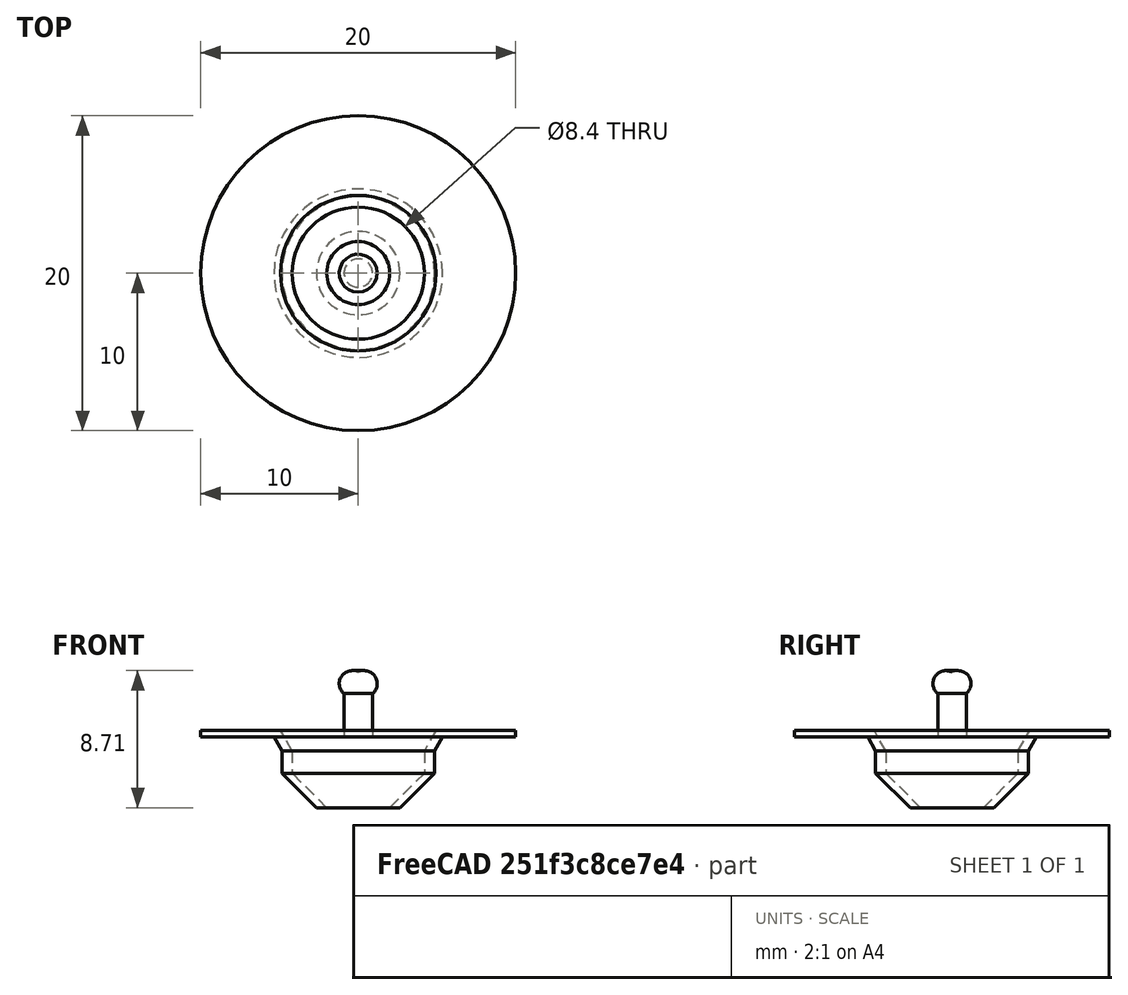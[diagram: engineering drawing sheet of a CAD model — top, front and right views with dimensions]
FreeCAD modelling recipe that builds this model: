
FCSTD DOCUMENT  (FreeCAD 0.15R4671 (Git))
Label: v4
License: CC-BY 3.0
LicenseURL: http://creativecommons.org/licenses/by/3.0/
objects: Sketcher::SketchObject×20, PartDesign::Revolution×14, App::MeasureDistance×2, Mesh::Feature×1, App::DocumentObjectGroup×1
note: 48 computed .brp shape members not serialized (recipe doc carries the construction recipe); baked Part::Feature solids carry a one-line shape summary decoded from their .brp

FEATURE [Mesh::Feature] M2_Electrode_Mount_B_01  label="M2_Electrode Mount B_01"
FEATURE [Sketcher::SketchObject] Sketch
  sketch-geometry (2):
    g0: Circle CenterX=0 CenterY=0 CenterZ=0 NormalX=0 NormalY=0 NormalZ=1 Radius=5.35
    g1: Circle CenterX=0 CenterY=0 CenterZ=0 NormalX=0 NormalY=0 NormalZ=1 Radius=10
  constraints (2):
    c: Coincident(g0,g-1)
    c: Coincident(g1,g-1)
FEATURE [Sketcher::SketchObject] Sketch001
  Placement = pos=(0,0,-0.9) rot=(0,0,1;0rad)
  sketch-geometry (1):
    g0: Circle CenterX=0 CenterY=0 CenterZ=0 NormalX=0 NormalY=0 NormalZ=1 Radius=4.85008
  constraints (1):
    c: Coincident(g0,g-1)
FEATURE [Sketcher::SketchObject] Sketch002
  Placement = pos=(0,0,-2.3) rot=(0,0,1;0rad)
  sketch-geometry (1):
    g0: Circle CenterX=0 CenterY=0 CenterZ=0 NormalX=0 NormalY=0 NormalZ=1 Radius=4.85
  constraints (1):
    c: Coincident(g0,g-1)
FEATURE [Sketcher::SketchObject] Sketch004
  Placement = pos=(0,0,-4.5) rot=(0,0,1;0rad)
  sketch-geometry (2):
    g0: Circle CenterX=0 CenterY=0 CenterZ=0 NormalX=0 NormalY=0 NormalZ=1 Radius=2.65073
    g1: Circle CenterX=0 CenterY=0 CenterZ=0 NormalX=0 NormalY=0 NormalZ=1 Radius=2.00003
  constraints (2):
    c: Coincident(g0,g-1)
    c: Coincident(g1,g-1)
FEATURE [Sketcher::SketchObject] Sketch005
  Placement = pos=(0,0,0) rot=(1,0,0;1.5708rad)
  sketch-geometry (10):
    g0: LineSegment StartX=2 StartY=-4.5 StartZ=0 EndX=2.65074 EndY=-4.5 EndZ=0
    g1: LineSegment StartX=2.65074 StartY=-4.5 StartZ=0 EndX=4.85006 EndY=-2.29993 EndZ=0
    g2: LineSegment StartX=4.85006 StartY=-2.29993 StartZ=0 EndX=4.85006 EndY=-0.900001 EndZ=0
    g3: LineSegment StartX=4.85006 StartY=-0.900001 StartZ=0 EndX=5.35009 EndY=0 EndZ=0
    g4: LineSegment StartX=5.35009 StartY=0 StartZ=0 EndX=10 EndY=0 EndZ=0
    g5: LineSegment StartX=10 StartY=0 StartZ=0 EndX=10 EndY=0.428388 EndZ=0
    g6: LineSegment StartX=10 StartY=0.428388 StartZ=0 EndX=4.93781 EndY=0.428388 EndZ=0
    g7: LineSegment StartX=4.93781 StartY=0.428388 StartZ=0 EndX=4.19944 EndY=-0.900596 EndZ=0
    g8: LineSegment StartX=4.19944 StartY=-0.900596 StartZ=0 EndX=4.19944 EndY=-2.29981 EndZ=0
    g9: LineSegment StartX=4.19944 StartY=-2.29981 StartZ=0 EndX=2 EndY=-4.5 EndZ=0
  constraints (28):
    c: Coincident(g0,g1)
    c: Coincident(g1,g2)
    c: Coincident(g2,g3)
    c: Coincident(g3,g4)
    c: Coincident(g4,g5)
    c: Coincident(g5,g6)
    c: Coincident(g6,g7)
    c: Coincident(g7,g8)
    c: Coincident(g8,g9)
    c: Coincident(g9,g0)
    c: Parallel(g6,g4)
    c: Parallel(g4,g0)
    c: Parallel(g5,g2)
    c: Parallel(g2,g8)
    c: Perpendicular(g0,g5)
    c: PointOnObject(g3,g-1)
    c: Parallel(g9,g1)
    c: Parallel(g7,g3)
    c: DistanceX(g0) = 2
    c: DistanceY(g0) = -4.5
    c: DistanceX(g4) = 10
    c: DistanceX(g0) = 2.65074
    c: DistanceY(g0) = -4.5
    c: DistanceX(g1) = 4.85006
    c: DistanceY(g1) = -2.29993
    c: DistanceY(g2) = -0.900001
    c: DistanceX(g3) = 5.35009
    c: DistanceX(g8) = 4.19944
FEATURE [PartDesign::Revolution] Revolution
  Angle = 360
  Axis = (0,0,1)
  Base = (0,0,0)
  Placement = pos=(0,0,0) rot=(1,0,0;1.5708rad)
  ReferenceAxis = -> Sketch005 [V_Axis]
  Reversed = true
  Sketch = -> Sketch005
FEATURE [App::MeasureDistance] Distance  label="Distance: 9.230"
  Distance = 9.23027
  P1 = (1.17962,4.49115,-0.0546159)
  P2 = (0.029117,-4.66704,-0.0122256)
FEATURE [App::MeasureDistance] Distance001  label="Distance: 0.441"
  Distance = 0.440793
  P1 = (9.09126,2.41844,0.428389)
  P2 = (9.11452,2.51963,3.00364e-07)
FEATURE [Sketcher::SketchObject] Sketch007
  Placement = pos=(7.73451,1.07818,-0.883026) rot=(-1,0,0;4.71239rad)
  sketch-geometry (5):
    g0: LineSegment StartX=-9.46196 StartY=0 StartZ=0 EndX=-8.29774 EndY=0 EndZ=0
    g1: LineSegment StartX=-8.29774 StartY=0 StartZ=0 EndX=-8.29774 EndY=3.88434 EndZ=0
    g2: LineSegment StartX=-8.29774 StartY=3.88434 StartZ=0 EndX=-9.46196 EndY=3.88434 EndZ=0
    g3: LineSegment StartX=-9.46196 StartY=3.88434 StartZ=0 EndX=-9.46196 EndY=0 EndZ=0
    g4: ArcOfCircle CenterX=-8.87985 CenterY=3.88434 CenterZ=0 NormalX=0 NormalY=0 NormalZ=1 Radius=0.582108 StartAngle=0 EndAngle=3.14159
  constraints (12):
    c: Coincident(g0,g1)
    c: Coincident(g1,g2)
    c: Coincident(g2,g3)
    c: Coincident(g3,g0)
    c: Horizontal(g0)
    c: Horizontal(g2)
    c: Vertical(g1)
    c: Vertical(g3)
    c: PointOnObject(g0,g-1)
    c: Coincident(g4,g2)
    c: Coincident(g4,g1)
    c: PointOnObject(g4,g2)
FEATURE [Sketcher::SketchObject] Sketch008
  Placement = pos=(-1.0987,1.62082,-1.41935) rot=(-1,0,0;4.71239rad)
  sketch-geometry (5):
    g0: LineSegment StartX=-6.89941 StartY=0 StartZ=0 EndX=-6.5302 EndY=0 EndZ=0
    g1: LineSegment StartX=-6.5302 StartY=0 StartZ=0 EndX=-6.5302 EndY=3.74273 EndZ=0
    g2: LineSegment StartX=-6.5302 StartY=3.74273 StartZ=0 EndX=-6.89941 EndY=2.8 EndZ=0
    g3: LineSegment StartX=-6.89941 StartY=2.8 StartZ=0 EndX=-6.89941 EndY=0 EndZ=0
    g4: ArcOfCircle CenterX=-6.71481 CenterY=3.27137 CenterZ=0 NormalX=0 NormalY=0 NormalZ=1 Radius=0.506226 StartAngle=1.19753 EndAngle=4.33912
  constraints (11):
    c: Coincident(g0,g1)
    c: Coincident(g1,g2)
    c: Coincident(g2,g3)
    c: Coincident(g3,g0)
    c: PointOnObject(g4,g2)
    c: PointOnObject(g0,g-1)
    c: PointOnObject(g0,g-1)
    c: Parallel(g1,g3)
    c: Coincident(g4,g1)
    c: Coincident(g4,g2)
    c: Perpendicular(g-1,g1)
FEATURE [Sketcher::SketchObject] Sketch021
  Placement = pos=(0,0,0) rot=(0.57735,0.57735,0.57735;2.0944rad)
  sketch-geometry (4):
    g0: LineSegment StartX=-0.902517 StartY=2.75014 StartZ=0 EndX=-0.902517 EndY=0 EndZ=0
    g1: LineSegment StartX=-0.902517 StartY=0 StartZ=0 EndX=0 EndY=0 EndZ=0
    g2: LineSegment StartX=0 StartY=0 StartZ=0 EndX=0 EndY=4.11565 EndZ=0
    g3: ArcOfCircle CenterX=-0.384781 CenterY=3.38896 CenterZ=0 NormalX=0 NormalY=0 NormalZ=1 Radius=0.822276 StartAngle=1.08383 EndAngle=4.0313
  constraints (8):
    c: Coincident(g0,g1)
    c: Coincident(g1,g2)
    c: Coincident(g3,g0)
    c: Coincident(g3,g2)
    c: PointOnObject(g2,g-2)
    c: Coincident(g1,g-1)
    c: PointOnObject(g0,g-1)
    c: Parallel(g0,g2)
FEATURE [PartDesign::Revolution] Revolution001
  Angle = 360
  Axis = (0,0,1)
  Base = (0,0,0)
  Placement = pos=(0,0,0) rot=(0.57735,0.57735,0.57735;2.0944rad)
  ReferenceAxis = -> Sketch021 [V_Axis]
  Sketch = -> Sketch021
FEATURE [Sketcher::SketchObject] Sketch022
  Placement = pos=(0,0,0) rot=(0.57735,0.57735,0.57735;2.0944rad)
  sketch-geometry (4):
    g0: LineSegment StartX=-0.902517 StartY=2.75014 StartZ=0 EndX=-0.902517 EndY=0 EndZ=0
    g1: LineSegment StartX=-0.902517 StartY=0 StartZ=0 EndX=0 EndY=0 EndZ=0
    g2: LineSegment StartX=0 StartY=0 StartZ=0 EndX=0 EndY=4.11565 EndZ=0
    g3: ArcOfCircle CenterX=-0.384781 CenterY=3.38896 CenterZ=0 NormalX=0 NormalY=0 NormalZ=1 Radius=0.822276 StartAngle=1.08383 EndAngle=4.0313
  constraints (8):
    c: Coincident(g0,g1)
    c: Coincident(g1,g2)
    c: Coincident(g3,g0)
    c: Coincident(g3,g2)
    c: PointOnObject(g2,g-2)
    c: Coincident(g1,g-1)
    c: PointOnObject(g0,g-1)
    c: Parallel(g0,g2)
FEATURE [PartDesign::Revolution] Revolution002
  Angle = 360
  Axis = (0,0,1)
  Base = (0,0,0)
  Placement = pos=(0,0,0) rot=(0.57735,0.57735,0.57735;2.0944rad)
  ReferenceAxis = -> Sketch022 [V_Axis]
  Sketch = -> Sketch022
FEATURE [Sketcher::SketchObject] Sketch023
  Placement = pos=(0,0,0) rot=(0.57735,0.57735,0.57735;2.0944rad)
  sketch-geometry (4):
    g0: LineSegment StartX=-0.902517 StartY=2.75014 StartZ=0 EndX=-0.902517 EndY=0 EndZ=0
    g1: LineSegment StartX=-0.902517 StartY=0 StartZ=0 EndX=0 EndY=0 EndZ=0
    g2: LineSegment StartX=0 StartY=0 StartZ=0 EndX=0 EndY=4.11565 EndZ=0
    g3: ArcOfCircle CenterX=-0.384781 CenterY=3.38896 CenterZ=0 NormalX=0 NormalY=0 NormalZ=1 Radius=0.822276 StartAngle=1.08383 EndAngle=4.0313
  constraints (8):
    c: Coincident(g0,g1)
    c: Coincident(g1,g2)
    c: Coincident(g3,g0)
    c: Coincident(g3,g2)
    c: PointOnObject(g2,g-2)
    c: Coincident(g1,g-1)
    c: PointOnObject(g0,g-1)
    c: Parallel(g0,g2)
FEATURE [PartDesign::Revolution] Revolution003
  Angle = 360
  Axis = (0,0,1)
  Base = (0,0,0)
  Placement = pos=(0,0,0) rot=(0.57735,0.57735,0.57735;2.0944rad)
  ReferenceAxis = -> Sketch023 [V_Axis]
  Sketch = -> Sketch023
FEATURE [Sketcher::SketchObject] Sketch024
  Placement = pos=(0,0,0) rot=(0.57735,0.57735,0.57735;2.0944rad)
  sketch-geometry (4):
    g0: LineSegment StartX=-0.902517 StartY=2.75014 StartZ=0 EndX=-0.902517 EndY=0 EndZ=0
    g1: LineSegment StartX=-0.902517 StartY=0 StartZ=0 EndX=0 EndY=0 EndZ=0
    g2: LineSegment StartX=0 StartY=0 StartZ=0 EndX=0 EndY=4.11565 EndZ=0
    g3: ArcOfCircle CenterX=-0.384781 CenterY=3.38896 CenterZ=0 NormalX=0 NormalY=0 NormalZ=1 Radius=0.822276 StartAngle=1.08383 EndAngle=4.0313
  constraints (8):
    c: Coincident(g0,g1)
    c: Coincident(g1,g2)
    c: Coincident(g3,g0)
    c: Coincident(g3,g2)
    c: PointOnObject(g2,g-2)
    c: Coincident(g1,g-1)
    c: PointOnObject(g0,g-1)
    c: Parallel(g0,g2)
FEATURE [PartDesign::Revolution] Revolution004
  Angle = 360
  Axis = (0,0,1)
  Base = (0,0,0)
  Placement = pos=(0,0,0) rot=(0.57735,0.57735,0.57735;2.0944rad)
  ReferenceAxis = -> Sketch024 [V_Axis]
  Sketch = -> Sketch024
FEATURE [Sketcher::SketchObject] Sketch025
  Placement = pos=(0,0,0) rot=(0.57735,0.57735,0.57735;2.0944rad)
  sketch-geometry (4):
    g0: LineSegment StartX=-0.902517 StartY=2.75014 StartZ=0 EndX=-0.902517 EndY=0 EndZ=0
    g1: LineSegment StartX=-0.902517 StartY=0 StartZ=0 EndX=0 EndY=0 EndZ=0
    g2: LineSegment StartX=0 StartY=0 StartZ=0 EndX=0 EndY=4.11565 EndZ=0
    g3: ArcOfCircle CenterX=-0.384781 CenterY=3.38896 CenterZ=0 NormalX=0 NormalY=0 NormalZ=1 Radius=0.822276 StartAngle=1.08383 EndAngle=4.0313
  constraints (8):
    c: Coincident(g0,g1)
    c: Coincident(g1,g2)
    c: Coincident(g3,g0)
    c: Coincident(g3,g2)
    c: PointOnObject(g2,g-2)
    c: Coincident(g1,g-1)
    c: PointOnObject(g0,g-1)
    c: Parallel(g0,g2)
FEATURE [PartDesign::Revolution] Revolution005
  Angle = 360
  Axis = (0,0,1)
  Base = (0,0,0)
  Placement = pos=(0,0,0) rot=(0.57735,0.57735,0.57735;2.0944rad)
  ReferenceAxis = -> Sketch025 [V_Axis]
  Sketch = -> Sketch025
FEATURE [Sketcher::SketchObject] Sketch026
  Placement = pos=(0,0,0) rot=(0.57735,0.57735,0.57735;2.0944rad)
  sketch-geometry (4):
    g0: LineSegment StartX=-0.902517 StartY=2.75014 StartZ=0 EndX=-0.902517 EndY=0 EndZ=0
    g1: LineSegment StartX=-0.902517 StartY=0 StartZ=0 EndX=0 EndY=0 EndZ=0
    g2: LineSegment StartX=0 StartY=0 StartZ=0 EndX=0 EndY=4.11565 EndZ=0
    g3: ArcOfCircle CenterX=-0.384781 CenterY=3.38896 CenterZ=0 NormalX=0 NormalY=0 NormalZ=1 Radius=0.822276 StartAngle=1.08383 EndAngle=4.0313
  constraints (8):
    c: Coincident(g0,g1)
    c: Coincident(g1,g2)
    c: Coincident(g3,g0)
    c: Coincident(g3,g2)
    c: PointOnObject(g2,g-2)
    c: Coincident(g1,g-1)
    c: PointOnObject(g0,g-1)
    c: Parallel(g0,g2)
FEATURE [PartDesign::Revolution] Revolution006
  Angle = 360
  Axis = (0,0,1)
  Base = (0,0,0)
  Placement = pos=(0,0,0) rot=(0.57735,0.57735,0.57735;2.0944rad)
  ReferenceAxis = -> Sketch026 [V_Axis]
  Sketch = -> Sketch026
FEATURE [Sketcher::SketchObject] Sketch027
  Placement = pos=(0,0,0) rot=(0.57735,0.57735,0.57735;2.0944rad)
  sketch-geometry (4):
    g0: LineSegment StartX=-0.902517 StartY=2.75014 StartZ=0 EndX=-0.902517 EndY=0 EndZ=0
    g1: LineSegment StartX=-0.902517 StartY=0 StartZ=0 EndX=0 EndY=0 EndZ=0
    g2: LineSegment StartX=0 StartY=0 StartZ=0 EndX=0 EndY=4.11565 EndZ=0
    g3: ArcOfCircle CenterX=-0.384781 CenterY=3.38896 CenterZ=0 NormalX=0 NormalY=0 NormalZ=1 Radius=0.822276 StartAngle=1.08383 EndAngle=4.0313
  constraints (8):
    c: Coincident(g0,g1)
    c: Coincident(g1,g2)
    c: Coincident(g3,g0)
    c: Coincident(g3,g2)
    c: PointOnObject(g2,g-2)
    c: Coincident(g1,g-1)
    c: PointOnObject(g0,g-1)
    c: Parallel(g0,g2)
FEATURE [PartDesign::Revolution] Revolution007
  Angle = 360
  Axis = (0,0,1)
  Base = (0,0,0)
  Placement = pos=(0,0,0) rot=(0.57735,0.57735,0.57735;2.0944rad)
  ReferenceAxis = -> Sketch027 [V_Axis]
  Sketch = -> Sketch027
FEATURE [Sketcher::SketchObject] Sketch028
  Placement = pos=(0,0,0) rot=(0.57735,0.57735,0.57735;2.0944rad)
  sketch-geometry (4):
    g0: LineSegment StartX=-0.902517 StartY=2.75014 StartZ=0 EndX=-0.902517 EndY=0 EndZ=0
    g1: LineSegment StartX=-0.902517 StartY=0 StartZ=0 EndX=0 EndY=0 EndZ=0
    g2: LineSegment StartX=0 StartY=0 StartZ=0 EndX=0 EndY=4.11565 EndZ=0
    g3: ArcOfCircle CenterX=-0.384781 CenterY=3.38896 CenterZ=0 NormalX=0 NormalY=0 NormalZ=1 Radius=0.822276 StartAngle=1.08383 EndAngle=4.0313
  constraints (8):
    c: Coincident(g0,g1)
    c: Coincident(g1,g2)
    c: Coincident(g3,g0)
    c: Coincident(g3,g2)
    c: PointOnObject(g2,g-2)
    c: Coincident(g1,g-1)
    c: PointOnObject(g0,g-1)
    c: Parallel(g0,g2)
FEATURE [PartDesign::Revolution] Revolution008
  Angle = 360
  Axis = (0,0,1)
  Base = (0,0,0)
  Placement = pos=(0,0,0) rot=(0.57735,0.57735,0.57735;2.0944rad)
  ReferenceAxis = -> Sketch028 [V_Axis]
  Sketch = -> Sketch028
FEATURE [Sketcher::SketchObject] Sketch029
  Placement = pos=(0,0,0) rot=(0.57735,0.57735,0.57735;2.0944rad)
  sketch-geometry (4):
    g0: LineSegment StartX=-0.902517 StartY=2.75014 StartZ=0 EndX=-0.902517 EndY=0 EndZ=0
    g1: LineSegment StartX=-0.902517 StartY=0 StartZ=0 EndX=0 EndY=0 EndZ=0
    g2: LineSegment StartX=0 StartY=0 StartZ=0 EndX=0 EndY=4.11565 EndZ=0
    g3: ArcOfCircle CenterX=-0.384781 CenterY=3.38896 CenterZ=0 NormalX=0 NormalY=0 NormalZ=1 Radius=0.822276 StartAngle=1.08383 EndAngle=4.0313
  constraints (8):
    c: Coincident(g0,g1)
    c: Coincident(g1,g2)
    c: Coincident(g3,g0)
    c: Coincident(g3,g2)
    c: PointOnObject(g2,g-2)
    c: Coincident(g1,g-1)
    c: PointOnObject(g0,g-1)
    c: Parallel(g0,g2)
FEATURE [PartDesign::Revolution] Revolution009
  Angle = 360
  Axis = (0,0,1)
  Base = (0,0,0)
  Placement = pos=(0,0,0) rot=(0.57735,0.57735,0.57735;2.0944rad)
  ReferenceAxis = -> Sketch029 [V_Axis]
  Sketch = -> Sketch029
FEATURE [Sketcher::SketchObject] Sketch030
  Placement = pos=(0,0,0) rot=(0.57735,0.57735,0.57735;2.0944rad)
  sketch-geometry (4):
    g0: LineSegment StartX=-0.902517 StartY=2.75014 StartZ=0 EndX=-0.902517 EndY=0 EndZ=0
    g1: LineSegment StartX=-0.902517 StartY=0 StartZ=0 EndX=0 EndY=0 EndZ=0
    g2: LineSegment StartX=0 StartY=0 StartZ=0 EndX=0 EndY=4.11565 EndZ=0
    g3: ArcOfCircle CenterX=-0.384781 CenterY=3.38896 CenterZ=0 NormalX=0 NormalY=0 NormalZ=1 Radius=0.822276 StartAngle=1.08383 EndAngle=4.0313
  constraints (8):
    c: Coincident(g0,g1)
    c: Coincident(g1,g2)
    c: Coincident(g3,g0)
    c: Coincident(g3,g2)
    c: PointOnObject(g2,g-2)
    c: Coincident(g1,g-1)
    c: PointOnObject(g0,g-1)
    c: Parallel(g0,g2)
FEATURE [PartDesign::Revolution] Revolution010
  Angle = 360
  Axis = (0,0,1)
  Base = (0,0,0)
  Placement = pos=(0,0,0) rot=(0.57735,0.57735,0.57735;2.0944rad)
  ReferenceAxis = -> Sketch030 [V_Axis]
  Sketch = -> Sketch030
FEATURE [Sketcher::SketchObject] Sketch031
  Placement = pos=(0,0,0) rot=(0.57735,0.57735,0.57735;2.0944rad)
  sketch-geometry (4):
    g0: LineSegment StartX=-0.902517 StartY=2.75014 StartZ=0 EndX=-0.902517 EndY=0 EndZ=0
    g1: LineSegment StartX=-0.902517 StartY=0 StartZ=0 EndX=0 EndY=0 EndZ=0
    g2: LineSegment StartX=0 StartY=0 StartZ=0 EndX=0 EndY=4.11565 EndZ=0
    g3: ArcOfCircle CenterX=-0.384781 CenterY=3.38896 CenterZ=0 NormalX=0 NormalY=0 NormalZ=1 Radius=0.822276 StartAngle=1.08383 EndAngle=4.0313
  constraints (8):
    c: Coincident(g0,g1)
    c: Coincident(g1,g2)
    c: Coincident(g3,g0)
    c: Coincident(g3,g2)
    c: PointOnObject(g2,g-2)
    c: Coincident(g1,g-1)
    c: PointOnObject(g0,g-1)
    c: Parallel(g0,g2)
FEATURE [PartDesign::Revolution] Revolution011
  Angle = 360
  Axis = (0,0,1)
  Base = (0,0,0)
  Placement = pos=(0,0,0) rot=(0.57735,0.57735,0.57735;2.0944rad)
  ReferenceAxis = -> Sketch031 [V_Axis]
  Sketch = -> Sketch031
FEATURE [Sketcher::SketchObject] Sketch032
  Placement = pos=(0,0,0) rot=(0.57735,0.57735,0.57735;2.0944rad)
  sketch-geometry (4):
    g0: LineSegment StartX=-0.902517 StartY=2.75014 StartZ=0 EndX=-0.902517 EndY=0 EndZ=0
    g1: LineSegment StartX=-0.902517 StartY=0 StartZ=0 EndX=0 EndY=0 EndZ=0
    g2: LineSegment StartX=0 StartY=0 StartZ=0 EndX=0 EndY=4.11565 EndZ=0
    g3: ArcOfCircle CenterX=-0.384781 CenterY=3.38896 CenterZ=0 NormalX=0 NormalY=0 NormalZ=1 Radius=0.822276 StartAngle=1.08383 EndAngle=4.0313
  constraints (8):
    c: Coincident(g0,g1)
    c: Coincident(g1,g2)
    c: Coincident(g3,g0)
    c: Coincident(g3,g2)
    c: PointOnObject(g2,g-2)
    c: Coincident(g1,g-1)
    c: PointOnObject(g0,g-1)
    c: Parallel(g0,g2)
FEATURE [PartDesign::Revolution] Revolution012
  Angle = 360
  Axis = (0,0,1)
  Base = (0,0,0)
  Placement = pos=(0,0,0) rot=(0.57735,0.57735,0.57735;2.0944rad)
  ReferenceAxis = -> Sketch032 [V_Axis]
  Sketch = -> Sketch032
FEATURE [Sketcher::SketchObject] Sketch033
  Placement = pos=(0,0,0) rot=(0.57735,0.57735,0.57735;2.0944rad)
  sketch-geometry (4):
    g0: LineSegment StartX=-0.902517 StartY=2.75014 StartZ=0 EndX=-0.902517 EndY=0 EndZ=0
    g1: LineSegment StartX=-0.902517 StartY=0 StartZ=0 EndX=0 EndY=0 EndZ=0
    g2: LineSegment StartX=0 StartY=0 StartZ=0 EndX=0 EndY=4.11565 EndZ=0
    g3: ArcOfCircle CenterX=-0.384781 CenterY=3.38896 CenterZ=0 NormalX=0 NormalY=0 NormalZ=1 Radius=0.822276 StartAngle=1.08383 EndAngle=4.0313
  constraints (8):
    c: Coincident(g0,g1)
    c: Coincident(g1,g2)
    c: Coincident(g3,g0)
    c: Coincident(g3,g2)
    c: PointOnObject(g2,g-2)
    c: Coincident(g1,g-1)
    c: PointOnObject(g0,g-1)
    c: Parallel(g0,g2)
FEATURE [PartDesign::Revolution] Revolution013
  Angle = 360
  Axis = (0,0,1)
  Base = (0,0,0)
  Placement = pos=(0,0,0) rot=(0.57735,0.57735,0.57735;2.0944rad)
  ReferenceAxis = -> Sketch033 [V_Axis]
  Sketch = -> Sketch033
FEATURE [App::DocumentObjectGroup] ____________001
  Group = -> [Revolution001,Revolution002,Revolution003,Revolution004,Revolution005,Revolution006,Revolution007,Revolution008,Revolution009,Revolution010,Revolution011,Revolution012,Revolution013]
